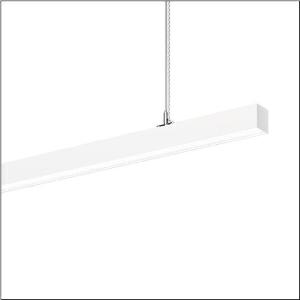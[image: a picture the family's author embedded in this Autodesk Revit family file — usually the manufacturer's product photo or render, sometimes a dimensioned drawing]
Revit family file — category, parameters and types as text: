
# Revit family: silica_r__21_51mx33da47wb_07b3
name_source: partatom
category: Lighting Fixtures
units: mm (PartAtom-declared; Revit-internal decimal feet)

## family parameters
Cut with Voids When Loaded = No
Host = Face
Light Source = No
Part Type = Normal
Room Calculation Point = No
Round Connector Dimension = Use Diameter
Shared = No

## types (1)
- --- (1 x LED, 5910 lm, 38.4 W, 4000K)
    Apparent Load = 38 VA
    CIE Flux Codes = 78 96 99 55 100
    Color Rendering = 80
    Color Temperature = 4000K
    Default Elevation = 1800 mm
    Description = Silica® 21, office luminaire, primary optical cover: prismatic diffuser, of PMMA, CAT 2 (L<= 3000cd/m²), light emission: direct/indirect distribution, primary light characteristic: symmetric, installation type: suspended mounting, LED, rated luminous flux: 5.910lm, luminous efficacy: 154lm/W, light colour: 840, colour temperature: 4000K, with terminal, 3+2-pole, max. 2.5mm², mains connection: 220..240V, AC, 50/60Hz, rated input power: 38.4W, luminaire housing, of aluminium, traffic white (RAL 9016), length: 1.204mm, width: 53mm, height: 53mm, protection rating (complete): IP20, insulation class (complete): insulation class I (protective earthing), certification: CE, permissible operating ambient temperature: 0..+35°C, standard: EN 50419, packaging unit: 1 piece
    Height = 53 mm
    Lamp = 1 x LED
    Lamp Light Flux = 5910 lm
    Lamp Power = 38.4 W
    Lamp count = 1
    Length = 1204 mm
    Luminous efficacy = 154 lm/W
    Manufacturer = Siteco
    ModVariant = No
    Model = 51MX33DA47WB
    Mounting Place = Ceiling
    Mounting Type = Pendant
    Number of Poles = 1
    OnlyDefault = Yes
    Power Factor = 1
    Product Name = Silica® 21
    Product group = office luminaire | ceiling pendant
    ProductGroupID = 902
    Protection Class = Protection class I
    Protection Degree = IP 20
    RLX_Detail_Level = 1
    RLX_Emergency_Light_Flux = 0 lm
    RLX_Emergency_Type = 0
    RLX_Emergency_Type_DB = No
    RlxData = <blob elided: 21153 chars, md5=cc03f76a>
    Socket = socket
    Standby Power = 0 W
    System Light Flux = 5910 lm
    System Power = 38 W
    Type Comments = factory setting: luminous flux: 100 % | dim-lin: 254 | 323 mA
    Type Image = l_1297784.jpg
    URL = http://relux.com
    VarID = @adj_049279
    Voltage = 0 V
    Weight = 0.00 kg
    Width = 53 mm

## geometry (parser evidence)
native form markers: Blend x4, Sweep x13
no freeform markers — native parametric forms only
